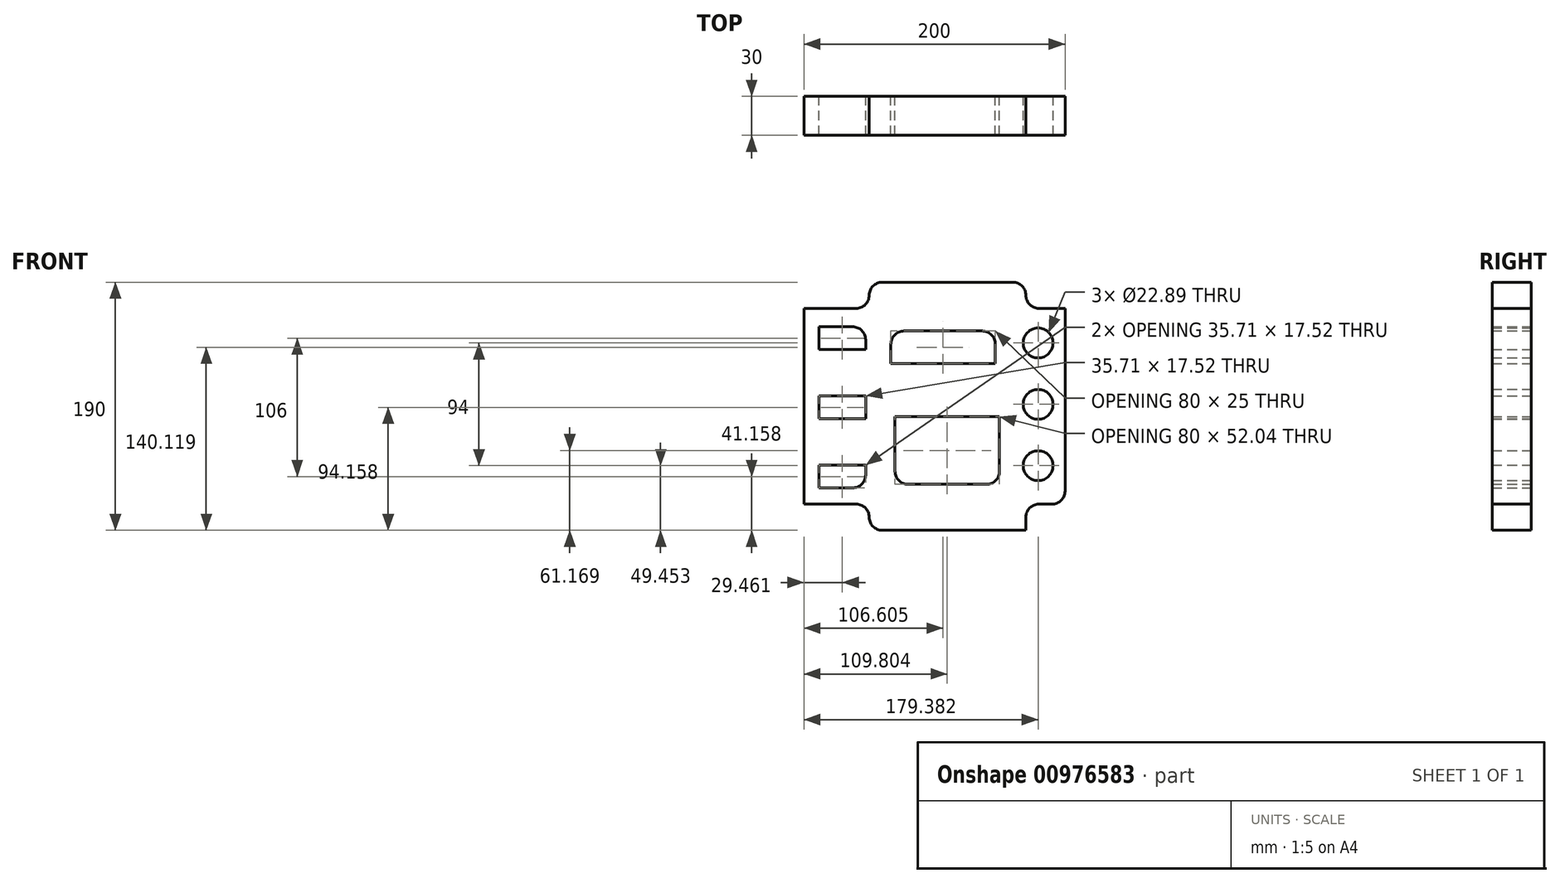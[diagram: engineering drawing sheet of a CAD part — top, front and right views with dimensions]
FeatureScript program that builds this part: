
annotation { "Feature Type Name" : "Feature", "Feature Type Description" : "" }
export const myFeature = defineFeature(function(context is Context, id is Id, definition is map)
    precondition{}
    {
        {
            var Q0;
            Q0=qCreatedBy(makeId("Front.planeOp"),FACE);
            var sketch = newSketch(context, id + "F0", { "sketchPlane" : qUnion([Q0])});
            skLineSegment(sketch, "E0", {"start": v(-21.74, 120.9) * mm, "end": v(78.26, 120.9) * mm});
            skLineSegment(sketch, "E1", {"start": v(-31.74, 110.9) * mm, "end": v(-31.74, 110.9) * mm});
            skLineSegment(sketch, "E2", {"start": v(-41.74, 100.9) * mm, "end": v(-81.74, 100.9) * mm});
            skLineSegment(sketch, "E3", {"start": v(-81.74, 100.9) * mm, "end": v(-81.74, -49.1) * mm});
            skLineSegment(sketch, "E4", {"start": v(-81.74, -49.1) * mm, "end": v(-41.74, -49.1) * mm});
            skLineSegment(sketch, "E5", {"start": v(-31.74, -59.1) * mm, "end": v(-31.74, -59.1) * mm});
            skLineSegment(sketch, "E6", {"start": v(-21.74, -69.1) * mm, "end": v(88.26, -69.1) * mm});
            skLineSegment(sketch, "E7", {"start": v(88.26, -69.1) * mm, "end": v(88.26, -59.1) * mm});
            skLineSegment(sketch, "E8", {"start": v(98.26, -49.1) * mm, "end": v(108.26, -49.1) * mm});
            skLineSegment(sketch, "E9", {"start": v(88.26, 110.9) * mm, "end": v(88.26, 110.9) * mm});
            skLineSegment(sketch, "E10", {"start": v(98.26, 100.9) * mm, "end": v(118.26, 100.9) * mm});
            skLineSegment(sketch, "E11", {"start": v(118.26, 100.9) * mm, "end": v(118.26, -39.1) * mm});
            skPoint(sketch, "E12.visualSharp", {"position": v(88.26, 120.9) * mm});
            skArc(sketch, "E12.filletArc", {"start": v(88.26, 110.9) * mm, "mid": v(85.33, 117.98) * mm, "end": v(78.26, 120.9) * mm});
            skPoint(sketch, "E13.visualSharp", {"position": v(88.26, 100.9) * mm});
            skArc(sketch, "E13.filletArc", {"start": v(88.26, 110.9) * mm, "mid": v(91.2, 103.84) * mm, "end": v(98.26, 100.9) * mm});
            skPoint(sketch, "E14.visualSharp", {"position": v(118.26, -49.1) * mm});
            skArc(sketch, "E14.filletArc", {"start": v(108.26, -49.1) * mm, "mid": v(115.33, -46.16) * mm, "end": v(118.26, -39.1) * mm});
            skPoint(sketch, "E15.visualSharp", {"position": v(88.26, -49.1) * mm});
            skArc(sketch, "E15.filletArc", {"start": v(98.26, -49.1) * mm, "mid": v(91.2, -52.02) * mm, "end": v(88.26, -59.1) * mm});
            skPoint(sketch, "E16.visualSharp", {"position": v(-31.74, -69.1) * mm});
            skArc(sketch, "E16.filletArc", {"start": v(-31.74, -59.1) * mm, "mid": v(-28.8, -66.16) * mm, "end": v(-21.74, -69.1) * mm});
            skPoint(sketch, "E17.visualSharp", {"position": v(-31.74, -49.1) * mm});
            skArc(sketch, "E17.filletArc", {"start": v(-31.74, -59.1) * mm, "mid": v(-34.67, -52.02) * mm, "end": v(-41.74, -49.1) * mm});
            skPoint(sketch, "E18.visualSharp", {"position": v(-31.74, 100.9) * mm});
            skArc(sketch, "E18.filletArc", {"start": v(-41.74, 100.9) * mm, "mid": v(-34.67, 103.84) * mm, "end": v(-31.74, 110.9) * mm});
            skPoint(sketch, "E19.visualSharp", {"position": v(-31.74, 120.9) * mm});
            skArc(sketch, "E19.filletArc", {"start": v(-21.74, 120.9) * mm, "mid": v(-28.8, 117.98) * mm, "end": v(-31.74, 110.9) * mm});
            skLineSegment(sketch, "E20.bottom", {"start": v(-70.13, 86.83) * mm, "end": v(-44.42, 86.83) * mm});
            skLineSegment(sketch, "E20.top", {"start": v(-70.13, 69.3) * mm, "end": v(-34.42, 69.3) * mm});
            skLineSegment(sketch, "E20.left", {"start": v(-70.13, 86.83) * mm, "end": v(-70.13, 69.3) * mm});
            skLineSegment(sketch, "E20.right", {"start": v(-34.42, 76.83) * mm, "end": v(-34.42, 69.3) * mm});
            skLineSegment(sketch, "E21.0.1.0", {"start": v(-70.13, 16.3) * mm, "end": v(-34.42, 16.3) * mm});
            skLineSegment(sketch, "E21.0.1.1", {"start": v(-34.42, 33.83) * mm, "end": v(-34.42, 16.3) * mm});
            skLineSegment(sketch, "E21.0.1.2", {"start": v(-70.13, 33.83) * mm, "end": v(-34.42, 33.83) * mm});
            skLineSegment(sketch, "E21.0.1.3", {"start": v(-70.13, 33.83) * mm, "end": v(-70.13, 16.3) * mm});
            skLineSegment(sketch, "E21.0.2.0", {"start": v(-70.13, -36.7) * mm, "end": v(-44.42, -36.7) * mm});
            skLineSegment(sketch, "E21.0.2.1", {"start": v(-34.42, -19.17) * mm, "end": v(-34.42, -26.7) * mm});
            skLineSegment(sketch, "E21.0.2.2", {"start": v(-70.13, -19.17) * mm, "end": v(-34.42, -19.17) * mm});
            skLineSegment(sketch, "E21.0.2.3", {"start": v(-70.13, -19.17) * mm, "end": v(-70.13, -36.7) * mm});
            skLineSegment(sketch, "E21.direction1", {"start": v(-70.13, 69.3) * mm, "end": v(-15.13, 69.3) * mm, "construction": true});
            skLineSegment(sketch, "E21.direction2", {"start": v(-70.13, 69.3) * mm, "end": v(-70.13, 16.3) * mm, "construction": true});
            skCircle(sketch, "E22", {"center": v(97.64, 74.36) * mm, "radius": 11.44 * mm});
            skCircle(sketch, "E23.0.1.0", {"center": v(97.64, 27.36) * mm, "radius": 11.44 * mm});
            skCircle(sketch, "E23.0.2.0", {"center": v(97.64, -19.64) * mm, "radius": 11.44 * mm});
            skLineSegment(sketch, "E23.direction1", {"start": v(97.64, 74.36) * mm, "end": v(69.64, 74.36) * mm, "construction": true});
            skLineSegment(sketch, "E23.direction2", {"start": v(97.64, 74.36) * mm, "end": v(97.64, 27.36) * mm, "construction": true});
            skLineSegment(sketch, "E24.bottom", {"start": v(-5.13, 83.53) * mm, "end": v(54.87, 83.53) * mm});
            skLineSegment(sketch, "E24.top", {"start": v(-15.13, 58.53) * mm, "end": v(64.87, 58.53) * mm});
            skLineSegment(sketch, "E24.left", {"start": v(-15.13, 73.53) * mm, "end": v(-15.13, 58.53) * mm});
            skLineSegment(sketch, "E24.right", {"start": v(64.87, 73.53) * mm, "end": v(64.87, 58.53) * mm});
            skLineSegment(sketch, "E25.bottom", {"start": v(-11.94, 18.1) * mm, "end": v(68.06, 18.1) * mm});
            skLineSegment(sketch, "E25.top", {"start": v(-1.94, -33.94) * mm, "end": v(58.06, -33.94) * mm});
            skLineSegment(sketch, "E25.left", {"start": v(-11.94, 18.1) * mm, "end": v(-11.94, -23.94) * mm});
            skLineSegment(sketch, "E25.right", {"start": v(68.06, 18.1) * mm, "end": v(68.06, -23.94) * mm});
            skPoint(sketch, "E26.visualSharp", {"position": v(-15.13, 83.53) * mm});
            skArc(sketch, "E26.filletArc", {"start": v(-5.13, 83.53) * mm, "mid": v(-12.2, 80.6) * mm, "end": v(-15.13, 73.53) * mm});
            skPoint(sketch, "E27.visualSharp", {"position": v(64.87, 83.53) * mm});
            skArc(sketch, "E27.filletArc", {"start": v(64.87, 73.53) * mm, "mid": v(61.94, 80.6) * mm, "end": v(54.87, 83.53) * mm});
            skPoint(sketch, "E28.visualSharp", {"position": v(-11.94, -33.94) * mm});
            skArc(sketch, "E28.filletArc", {"start": v(-11.94, -23.94) * mm, "mid": v(-9, -31.01) * mm, "end": v(-1.94, -33.94) * mm});
            skPoint(sketch, "E29.visualSharp", {"position": v(68.06, -33.94) * mm});
            skArc(sketch, "E29.filletArc", {"start": v(58.06, -33.94) * mm, "mid": v(65.14, -31.01) * mm, "end": v(68.06, -23.94) * mm});
            skPoint(sketch, "E30.visualSharp", {"position": v(-34.42, -36.7) * mm});
            skArc(sketch, "E30.filletArc", {"start": v(-44.42, -36.7) * mm, "mid": v(-37.35, -33.76) * mm, "end": v(-34.42, -26.7) * mm});
            skPoint(sketch, "E31.visualSharp", {"position": v(-34.42, 86.83) * mm});
            skArc(sketch, "E31.filletArc", {"start": v(-34.42, 76.83) * mm, "mid": v(-37.35, 83.9) * mm, "end": v(-44.42, 86.83) * mm});
            skSolve(sketch);
        }
        {
            var Q0;
            Q0 = qSketchRegion(id + "F0", true);
            extrude(context, id + "F1", {"entities" : qUnion([Q0]), "depth" : 30 * mm, "offsetDistance" : 25 * mm});
        }
    });
